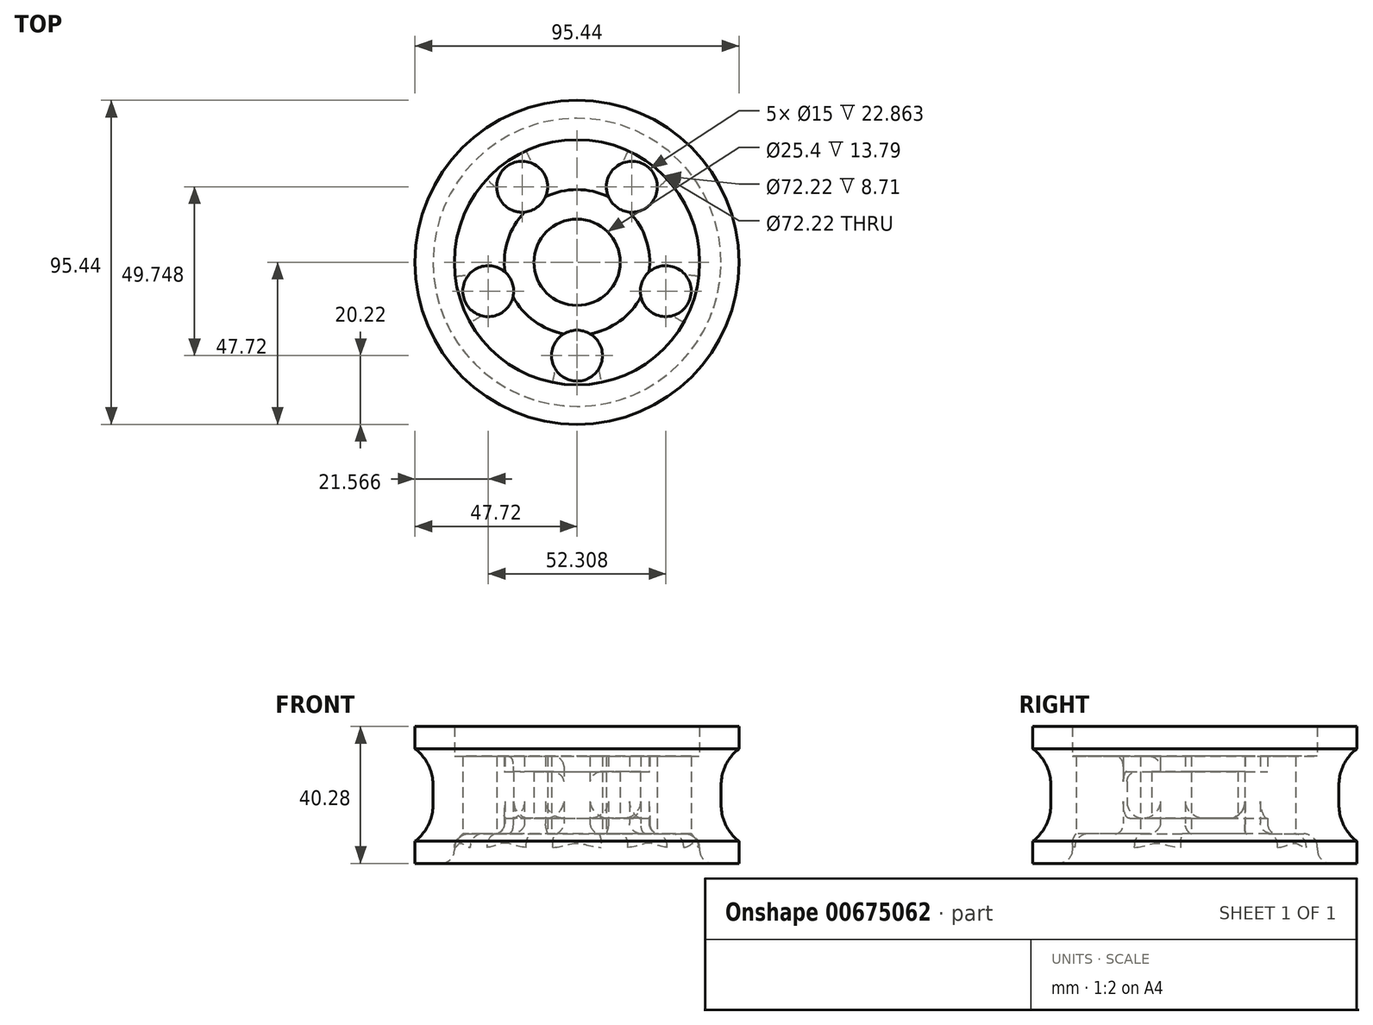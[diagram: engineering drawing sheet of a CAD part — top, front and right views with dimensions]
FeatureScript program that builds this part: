
annotation { "Feature Type Name" : "Feature", "Feature Type Description" : "" }
export const myFeature = defineFeature(function(context is Context, id is Id, definition is map)
    precondition{}
    {
        {
            var Q0;
            Q0=qCreatedBy(makeId("Front.planeOp"),FACE);
            var sketch = newSketch(context, id + "F0", { "sketchPlane" : qUnion([Q0])});
            skLineSegment(sketch, "E0", {"start": v(-72.4, 20.14) * mm, "end": v(-3.63, 20.14) * mm, "construction": true});
            skLineSegment(sketch, "E1", {"start": v(-12.7, 20.14) * mm, "end": v(-12.7, 27.04) * mm});
            skLineSegment(sketch, "E2", {"start": v(-12.7, 27.04) * mm, "end": v(-21.41, 27.04) * mm});
            skLineSegment(sketch, "E3", {"start": v(-21.41, 27.04) * mm, "end": v(-21.41, 31.57) * mm});
            skLineSegment(sketch, "E4", {"start": v(-21.41, 31.57) * mm, "end": v(-36.1, 31.57) * mm});
            skLineSegment(sketch, "E5", {"start": v(-36.1, 31.57) * mm, "end": v(-36.1, 40.28) * mm});
            skLineSegment(sketch, "E6", {"start": v(-36.1, 40.28) * mm, "end": v(-47.72, 40.28) * mm});
            skLineSegment(sketch, "E7", {"start": v(-47.72, 40.28) * mm, "end": v(-47.72, 33.75) * mm});
            skLineSegment(sketch, "E8", {"start": v(-47.72, 33.75) * mm, "end": v(-42.43, 33.75) * mm});
            skLineSegment(sketch, "E9", {"start": v(-42.43, 33.75) * mm, "end": v(-42.43, 20.14) * mm});
            skLineSegment(sketch, "E10.MirrorCS", {"start": v(-21.41, 13.25) * mm, "end": v(-21.41, 8.7) * mm});
            skLineSegment(sketch, "E11.MirrorCS", {"start": v(-12.7, 20.14) * mm, "end": v(-12.7, 13.25) * mm});
            skLineSegment(sketch, "E12.MirrorCS", {"start": v(-12.7, 13.25) * mm, "end": v(-21.41, 13.25) * mm});
            skLineSegment(sketch, "E13.MirrorCS", {"start": v(-36.1, 0) * mm, "end": v(-47.72, 0) * mm});
            skLineSegment(sketch, "E14.MirrorCS", {"start": v(-47.72, 0) * mm, "end": v(-47.72, 6.53) * mm});
            skLineSegment(sketch, "E15.MirrorCS", {"start": v(-42.43, 6.53) * mm, "end": v(-42.43, 20.14) * mm});
            skLineSegment(sketch, "E16.MirrorCS", {"start": v(-21.41, 8.7) * mm, "end": v(-36.1, 8.7) * mm});
            skLineSegment(sketch, "E17.MirrorCS", {"start": v(-47.72, 6.53) * mm, "end": v(-42.43, 6.53) * mm});
            skLineSegment(sketch, "E18.MirrorCS", {"start": v(-36.1, 8.7) * mm, "end": v(-36.1, 0) * mm});
            skLineSegment(sketch, "E19", {"start": v(0, 8.35) * mm, "end": v(0, 40.65) * mm, "construction": true});
            skLineSegment(sketch, "E20", {"start": v(-36.1, 0) * mm, "end": v(0, 0) * mm, "construction": true});
            skSolve(sketch);
        }
        {
            var Q0;
            Q0=makeQuery(id+"F0.imprint","IMPRINT",FACE,{"disambiguationData":[TD([[makeQuery(id+"F0.imprint","IMPRINT",EDGE,{"derivedFrom":sQuery(id+"F0.wireOp",EDGE,"E1")}),1.0]])]});
            var Q1;
            Q1=sQuery(id+"F0.wireOp",EDGE,"E19");
            revolve(context, id + "F1", {"entities" : qUnion([Q0]), "axis" : qUnion([Q1]), "revolveType" : RevolveType.FULL});
        }
        {
            var Q0;
            Q0=makeQuery(id+"F1.opRevolve","SWEPT_FACE",FACE,{"disambiguationData":[OSD([sQuery(id+"F0.wireOp",EDGE,"E9"),sQuery(id+"F0.wireOp",EDGE,"E15.MirrorCS")])]});
            fillet(context, id + "F2", {"entities" : qUnion([Q0]), "radius" : (27 / 2) * mm, "tangentPropagation" : true, "allowEdgeOverflow" : false});
        }
        {
            var Q0;
            Q0=qCreatedBy(makeId("Top.planeOp"),FACE);
            var sketch = newSketch(context, id + "F3", { "sketchPlane" : qUnion([Q0])});
            skCircle(sketch, "E21", {"center": v(0, 0) * mm, "radius": 35 * mm, "construction": true});
            skCircle(sketch, "E22", {"center": v(0, 0) * mm, "radius": 20 * mm, "construction": true});
            skLineSegment(sketch, "E23", {"start": v(0, -20) * mm, "end": v(0, -35) * mm, "construction": true});
            skCircle(sketch, "E24", {"center": v(0, -27.5) * mm, "radius": 7.5 * mm});
            skCircle(sketch, "E25.1.0", {"center": v(26.15, -8.5) * mm, "radius": 7.5 * mm});
            skCircle(sketch, "E25.2.0", {"center": v(16.16, 22.25) * mm, "radius": 7.5 * mm});
            skCircle(sketch, "E25.3.0", {"center": v(-16.16, 22.25) * mm, "radius": 7.5 * mm});
            skCircle(sketch, "E25.4.0", {"center": v(-26.15, -8.5) * mm, "radius": 7.5 * mm});
            skSolve(sketch);
        }
        {
            var Q0;
            Q0 = qSketchRegion(id + "F3", true);
            extrude(context, id + "F4", {"entities" : qUnion([Q0]), "operationType" : NewBodyOperationType.REMOVE, "depth" : 68.6 * mm, "offsetDistance" : 25 * mm});
        }
        {
            var Q0;
            Q0=makeQuery(id+"F1.opRevolve","SWEPT_EDGE",EDGE,{"disambiguationData":[OSD([sQuery(id+"F0.wireOp",EDGE,"E13.MirrorCS"),sQuery(id+"F0.wireOp",EDGE,"E18.MirrorCS")])]});
            var Q1;
            Q1=makeQuery(id+"F1.opRevolve","SWEPT_EDGE",EDGE,{"disambiguationData":[OSD([sQuery(id+"F0.wireOp",EDGE,"E16.MirrorCS"),sQuery(id+"F0.wireOp",EDGE,"E18.MirrorCS")])]});
            fillet(context, id + "F5", {"entities" : qUnion([Q0, Q1]), "radius" : 4 * mm, "tangentPropagation" : true, "allowEdgeOverflow" : false});
        }
        {
            var Q0;
            {var subQ0=sQuery(id+"F0.wireOp",EDGE,"E10.MirrorCS");var subQ1=sQuery(id+"F0.wireOp",EDGE,"E16.MirrorCS");Q0=makeQuery(id+"F4.boolean.opBoolean","SPLIT",EDGE,{"disambiguationData":[TD([makeQuery(id+"F1.opRevolve","SWEPT_FACE",FACE,{"disambiguationData":[OSD([subQ0])]}),makeQuery(id+"F1.opRevolve","SWEPT_FACE",FACE,{"disambiguationData":[OSD([subQ1])]}),makeQuery(id+"F4.opExtrude","SWEPT_FACE",FACE,{"disambiguationData":[OSD([sQuery(id+"F3.wireOp",EDGE,"E24")])]}),makeQuery(id+"F4.opExtrude","SWEPT_FACE",FACE,{"disambiguationData":[OSD([sQuery(id+"F3.wireOp",EDGE,"E25.1.0")])]})])],"derivedFrom":makeQuery(id+"F1.opRevolve","SWEPT_EDGE",EDGE,{"disambiguationData":[OSD([subQ0,subQ1])]})});}
            var Q1;
            {var subQ0=sQuery(id+"F0.wireOp",EDGE,"E10.MirrorCS");var subQ1=sQuery(id+"F0.wireOp",EDGE,"E16.MirrorCS");Q1=makeQuery(id+"F4.boolean.opBoolean","SPLIT",EDGE,{"disambiguationData":[TD([makeQuery(id+"F1.opRevolve","SWEPT_FACE",FACE,{"disambiguationData":[OSD([subQ0])]}),makeQuery(id+"F1.opRevolve","SWEPT_FACE",FACE,{"disambiguationData":[OSD([subQ1])]}),makeQuery(id+"F4.opExtrude","SWEPT_FACE",FACE,{"disambiguationData":[OSD([sQuery(id+"F3.wireOp",EDGE,"E25.1.0")])]}),makeQuery(id+"F4.opExtrude","SWEPT_FACE",FACE,{"disambiguationData":[OSD([sQuery(id+"F3.wireOp",EDGE,"E25.2.0")])]})])],"derivedFrom":makeQuery(id+"F1.opRevolve","SWEPT_EDGE",EDGE,{"disambiguationData":[OSD([subQ0,subQ1])]})});}
            var Q2;
            {var subQ0=sQuery(id+"F0.wireOp",EDGE,"E10.MirrorCS");var subQ1=sQuery(id+"F0.wireOp",EDGE,"E16.MirrorCS");Q2=makeQuery(id+"F4.boolean.opBoolean","SPLIT",EDGE,{"disambiguationData":[TD([makeQuery(id+"F1.opRevolve","SWEPT_FACE",FACE,{"disambiguationData":[OSD([subQ0])]}),makeQuery(id+"F1.opRevolve","SWEPT_FACE",FACE,{"disambiguationData":[OSD([subQ1])]}),makeQuery(id+"F4.opExtrude","SWEPT_FACE",FACE,{"disambiguationData":[OSD([sQuery(id+"F3.wireOp",EDGE,"E25.2.0")])]}),makeQuery(id+"F4.opExtrude","SWEPT_FACE",FACE,{"disambiguationData":[OSD([sQuery(id+"F3.wireOp",EDGE,"E25.3.0")])]})])],"derivedFrom":makeQuery(id+"F1.opRevolve","SWEPT_EDGE",EDGE,{"disambiguationData":[OSD([subQ0,subQ1])]})});}
            var Q3;
            {var subQ0=sQuery(id+"F0.wireOp",EDGE,"E10.MirrorCS");var subQ1=sQuery(id+"F0.wireOp",EDGE,"E16.MirrorCS");Q3=makeQuery(id+"F4.boolean.opBoolean","SPLIT",EDGE,{"disambiguationData":[TD([makeQuery(id+"F1.opRevolve","SWEPT_FACE",FACE,{"disambiguationData":[OSD([subQ0])]}),makeQuery(id+"F1.opRevolve","SWEPT_FACE",FACE,{"disambiguationData":[OSD([subQ1])]}),makeQuery(id+"F4.opExtrude","SWEPT_FACE",FACE,{"disambiguationData":[OSD([sQuery(id+"F3.wireOp",EDGE,"E24")])]}),makeQuery(id+"F4.opExtrude","SWEPT_FACE",FACE,{"disambiguationData":[OSD([sQuery(id+"F3.wireOp",EDGE,"E25.4.0")])]})])],"derivedFrom":makeQuery(id+"F1.opRevolve","SWEPT_EDGE",EDGE,{"disambiguationData":[OSD([subQ0,subQ1])]})});}
            var Q4;
            {var subQ0=sQuery(id+"F0.wireOp",EDGE,"E10.MirrorCS");var subQ1=sQuery(id+"F0.wireOp",EDGE,"E16.MirrorCS");Q4=makeQuery(id+"F4.boolean.opBoolean","SPLIT",EDGE,{"disambiguationData":[TD([makeQuery(id+"F1.opRevolve","SWEPT_FACE",FACE,{"disambiguationData":[OSD([subQ0])]}),makeQuery(id+"F1.opRevolve","SWEPT_FACE",FACE,{"disambiguationData":[OSD([subQ1])]}),makeQuery(id+"F4.opExtrude","SWEPT_FACE",FACE,{"disambiguationData":[OSD([sQuery(id+"F3.wireOp",EDGE,"E25.3.0")])]}),makeQuery(id+"F4.opExtrude","SWEPT_FACE",FACE,{"disambiguationData":[OSD([sQuery(id+"F3.wireOp",EDGE,"E25.4.0")])]})])],"derivedFrom":makeQuery(id+"F1.opRevolve","SWEPT_EDGE",EDGE,{"disambiguationData":[OSD([subQ0,subQ1])]})});}
            fillet(context, id + "F6", {"entities" : qUnion([Q0, Q1, Q2, Q3, Q4]), "radius" : 3 * mm, "tangentPropagation" : true, "allowEdgeOverflow" : false});
        }
        {
            var Q0;
            Q0=makeQuery(id+"F4.boolean.opBoolean","INTERSECT",EDGE,{"derivedFrom":[makeQuery(id+"F1.opRevolve","SWEPT_FACE",FACE,{"disambiguationData":[OSD([sQuery(id+"F0.wireOp",EDGE,"E12.MirrorCS")])]}),makeQuery(id+"F4.opExtrude","SWEPT_FACE",FACE,{"disambiguationData":[OSD([sQuery(id+"F3.wireOp",EDGE,"E25.1.0")])]})]});
            var Q1;
            Q1=makeQuery(id+"F4.boolean.opBoolean","INTERSECT",EDGE,{"derivedFrom":[makeQuery(id+"F1.opRevolve","SWEPT_FACE",FACE,{"disambiguationData":[OSD([sQuery(id+"F0.wireOp",EDGE,"E12.MirrorCS")])]}),makeQuery(id+"F4.opExtrude","SWEPT_FACE",FACE,{"disambiguationData":[OSD([sQuery(id+"F3.wireOp",EDGE,"E24")])]})]});
            var Q2;
            Q2=makeQuery(id+"F4.boolean.opBoolean","INTERSECT",EDGE,{"derivedFrom":[makeQuery(id+"F1.opRevolve","SWEPT_FACE",FACE,{"disambiguationData":[OSD([sQuery(id+"F0.wireOp",EDGE,"E12.MirrorCS")])]}),makeQuery(id+"F4.opExtrude","SWEPT_FACE",FACE,{"disambiguationData":[OSD([sQuery(id+"F3.wireOp",EDGE,"E25.4.0")])]})]});
            var Q3;
            Q3=makeQuery(id+"F4.boolean.opBoolean","INTERSECT",EDGE,{"derivedFrom":[makeQuery(id+"F1.opRevolve","SWEPT_FACE",FACE,{"disambiguationData":[OSD([sQuery(id+"F0.wireOp",EDGE,"E12.MirrorCS")])]}),makeQuery(id+"F4.opExtrude","SWEPT_FACE",FACE,{"disambiguationData":[OSD([sQuery(id+"F3.wireOp",EDGE,"E25.3.0")])]})]});
            var Q4;
            Q4=makeQuery(id+"F4.boolean.opBoolean","INTERSECT",EDGE,{"derivedFrom":[makeQuery(id+"F1.opRevolve","SWEPT_FACE",FACE,{"disambiguationData":[OSD([sQuery(id+"F0.wireOp",EDGE,"E12.MirrorCS")])]}),makeQuery(id+"F4.opExtrude","SWEPT_FACE",FACE,{"disambiguationData":[OSD([sQuery(id+"F3.wireOp",EDGE,"E25.2.0")])]})]});
            fillet(context, id + "F7", {"entities" : qUnion([Q0, Q1, Q2, Q3, Q4]), "radius" : 5 * mm, "tangentPropagation" : true, "allowEdgeOverflow" : false});
        }
        {
            var Q0;
            Q0=makeQuery(id+"F4.boolean.opBoolean","INTERSECT",EDGE,{"derivedFrom":[makeQuery(id+"F1.opRevolve","SWEPT_FACE",FACE,{"disambiguationData":[OSD([sQuery(id+"F0.wireOp",EDGE,"E2")])]}),makeQuery(id+"F4.opExtrude","SWEPT_FACE",FACE,{"disambiguationData":[OSD([sQuery(id+"F3.wireOp",EDGE,"E24")])]})]});
            var Q1;
            {var subQ0=sQuery(id+"F0.wireOp",EDGE,"E3");var subQ1=sQuery(id+"F0.wireOp",EDGE,"E4");Q1=makeQuery(id+"F4.boolean.opBoolean","SPLIT",EDGE,{"disambiguationData":[TD([makeQuery(id+"F1.opRevolve","SWEPT_FACE",FACE,{"disambiguationData":[OSD([subQ0])]}),makeQuery(id+"F1.opRevolve","SWEPT_FACE",FACE,{"disambiguationData":[OSD([subQ1])]}),makeQuery(id+"F4.opExtrude","SWEPT_FACE",FACE,{"disambiguationData":[OSD([sQuery(id+"F3.wireOp",EDGE,"E24")])]}),makeQuery(id+"F4.opExtrude","SWEPT_FACE",FACE,{"disambiguationData":[OSD([sQuery(id+"F3.wireOp",EDGE,"E25.4.0")])]})])],"derivedFrom":makeQuery(id+"F1.opRevolve","SWEPT_EDGE",EDGE,{"disambiguationData":[OSD([subQ0,subQ1])]})});}
            fillet(context, id + "F8", {"entities" : qUnion([Q0, Q1]), "radius" : 3 * mm, "tangentPropagation" : true, "allowEdgeOverflow" : false});
        }
    });
